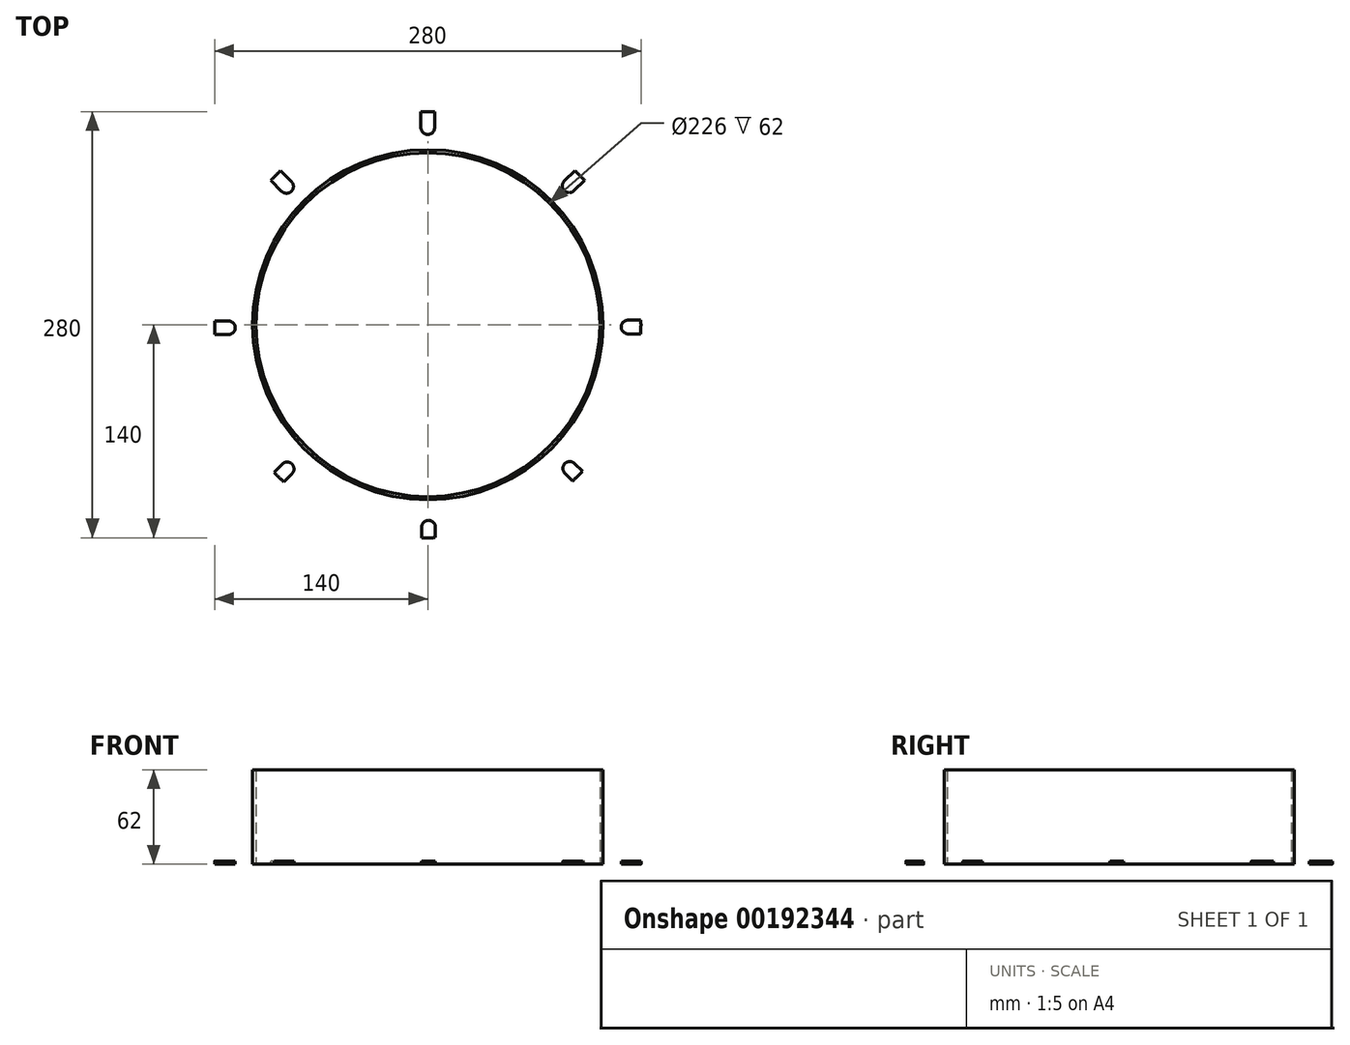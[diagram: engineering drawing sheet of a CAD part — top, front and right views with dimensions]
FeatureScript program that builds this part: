
annotation { "Feature Type Name" : "Feature", "Feature Type Description" : "" }
export const myFeature = defineFeature(function(context is Context, id is Id, definition is map)
    precondition{}
    {
        {
            var Q0;
            Q0=qCreatedBy(makeId("Top.planeOp"),FACE);
            var sketch = newSketch(context, id + "F0", { "sketchPlane" : qUnion([Q0])});
            skCircle(sketch, "E0", {"center": v(0, 0) * mm, "radius": 140 * mm});
            skCircle(sketch, "E1", {"center": v(0, 0) * mm, "radius": 113 * mm});
            skSolve(sketch);
        }
        {
            var Q0;
            Q0=makeQuery(id+"F0.imprint","IMPRINT",FACE,{"disambiguationData":[TD([[makeQuery(id+"F0.imprint","IMPRINT",EDGE,{"derivedFrom":sQuery(id+"F0.wireOp",EDGE,"E0")}),1.0]])]});
            extrude(context, id + "F1", {"entities" : qUnion([Q0]), "depth" : 2 * mm});
        }
        {
            var Q0;
            Q0=makeQuery(id+"F1.opExtrude","CAP_FACE",FACE,{"disambiguationData":[OSD([sQuery(id+"F0.wireOp",EDGE,"E0"),sQuery(id+"F0.wireOp",EDGE,"E1")])],"isStart":false});
            var sketch = newSketch(context, id + "F2", { "sketchPlane" : qUnion([Q0])});
            skCircle(sketch, "E2.0", {"center": v(0, 0) * mm, "radius": 113 * mm});
            skCircle(sketch, "E3.0", {"center": v(0, 0) * mm, "radius": 115 * mm});
            skSolve(sketch);
        }
        {
            var Q0;
            Q0=makeQuery(id+"F2.imprint","IMPRINT",FACE,{"disambiguationData":[TD([[makeQuery(id+"F2.imprint","IMPRINT",EDGE,{"derivedFrom":sQuery(id+"F2.wireOp",EDGE,"E2.0")}),-1.0]])]});
            extrude(context, id + "F3", {"entities" : qUnion([Q0]), "operationType" : NewBodyOperationType.ADD, "depth" : 60 * mm});
        }
        {
            var Q0;
            Q0=makeQuery(id+"F1.opExtrude","CAP_FACE",FACE,{"disambiguationData":[OSD([sQuery(id+"F0.wireOp",EDGE,"E0"),sQuery(id+"F0.wireOp",EDGE,"E1")])],"isStart":false});
            var sketch = newSketch(context, id + "F4", { "sketchPlane" : qUnion([Q0])});
            skLineSegment(sketch, "E4", {"start": v(0, 129.5) * mm, "end": v(0, 140) * mm});
            skArc(sketch, "E5.0.startCap", {"start": v(4.5, 129.5) * mm, "mid": v(0, 125) * mm, "end": v(-4.5, 129.5) * mm});
            skArc(sketch, "E5.0.endCap", {"start": v(-4.5, 140) * mm, "mid": v(0, 144.5) * mm, "end": v(4.5, 140) * mm});
            skLineSegment(sketch, "E5.0.left", {"start": v(-4.5, 129.5) * mm, "end": v(-4.5, 140) * mm});
            skLineSegment(sketch, "E5.0.right", {"start": v(4.5, 129.5) * mm, "end": v(4.5, 140) * mm});
            skArc(sketch, "E6.1.0", {"start": v(-103.34, 95.12) * mm, "mid": v(-103.34, 101.49) * mm, "end": v(-96.98, 101.49) * mm});
            skLineSegment(sketch, "E6.1.1", {"start": v(-89.55, 94.06) * mm, "end": v(-96.98, 101.49) * mm});
            skArc(sketch, "E6.1.2", {"start": v(-89.55, 94.06) * mm, "mid": v(-89.55, 87.7) * mm, "end": v(-95.92, 87.7) * mm});
            skLineSegment(sketch, "E6.1.3", {"start": v(-95.92, 87.7) * mm, "end": v(-103.34, 95.12) * mm});
            skArc(sketch, "E6.2.0", {"start": v(-141.5, -6.5) * mm, "mid": v(-146, -2) * mm, "end": v(-141.5, 2.5) * mm});
            skLineSegment(sketch, "E6.2.1", {"start": v(-131, 2.5) * mm, "end": v(-141.5, 2.5) * mm});
            skArc(sketch, "E6.2.2", {"start": v(-131, 2.5) * mm, "mid": v(-126.5, -2) * mm, "end": v(-131, -6.5) * mm});
            skLineSegment(sketch, "E6.2.3", {"start": v(-131, -6.5) * mm, "end": v(-141.5, -6.5) * mm});
            skArc(sketch, "E6.3.0", {"start": v(-96.62, -105.34) * mm, "mid": v(-102.99, -105.34) * mm, "end": v(-102.99, -98.98) * mm});
            skLineSegment(sketch, "E6.3.1", {"start": v(-95.56, -91.55) * mm, "end": v(-102.99, -98.98) * mm});
            skArc(sketch, "E6.3.2", {"start": v(-95.56, -91.55) * mm, "mid": v(-89.2, -91.55) * mm, "end": v(-89.2, -97.92) * mm});
            skLineSegment(sketch, "E6.3.3", {"start": v(-89.2, -97.92) * mm, "end": v(-96.62, -105.34) * mm});
            skArc(sketch, "E6.4.0", {"start": v(5, -143.5) * mm, "mid": v(0.5, -148) * mm, "end": v(-4, -143.5) * mm});
            skLineSegment(sketch, "E6.4.1", {"start": v(-4, -133) * mm, "end": v(-4, -143.5) * mm});
            skArc(sketch, "E6.4.2", {"start": v(-4, -133) * mm, "mid": v(0.5, -128.5) * mm, "end": v(5, -133) * mm});
            skLineSegment(sketch, "E6.4.3", {"start": v(5, -133) * mm, "end": v(5, -143.5) * mm});
            skArc(sketch, "E6.5.0", {"start": v(103.84, -98.62) * mm, "mid": v(103.84, -104.99) * mm, "end": v(97.48, -104.99) * mm});
            skLineSegment(sketch, "E6.5.1", {"start": v(90.05, -97.56) * mm, "end": v(97.48, -104.99) * mm});
            skArc(sketch, "E6.5.2", {"start": v(90.05, -97.56) * mm, "mid": v(90.05, -91.2) * mm, "end": v(96.42, -91.2) * mm});
            skLineSegment(sketch, "E6.5.3", {"start": v(96.42, -91.2) * mm, "end": v(103.84, -98.62) * mm});
            skArc(sketch, "E6.6.0", {"start": v(142, 3) * mm, "mid": v(146.5, -1.5) * mm, "end": v(142, -6) * mm});
            skLineSegment(sketch, "E6.6.1", {"start": v(131.5, -6) * mm, "end": v(142, -6) * mm});
            skArc(sketch, "E6.6.2", {"start": v(131.5, -6) * mm, "mid": v(127, -1.5) * mm, "end": v(131.5, 3) * mm});
            skLineSegment(sketch, "E6.6.3", {"start": v(131.5, 3) * mm, "end": v(142, 3) * mm});
            skArc(sketch, "E6.7.0", {"start": v(97.12, 101.84) * mm, "mid": v(103.49, 101.84) * mm, "end": v(103.49, 95.48) * mm});
            skLineSegment(sketch, "E6.7.1", {"start": v(96.06, 88.05) * mm, "end": v(103.49, 95.48) * mm});
            skArc(sketch, "E6.7.2", {"start": v(96.06, 88.05) * mm, "mid": v(89.7, 88.05) * mm, "end": v(89.7, 94.42) * mm});
            skLineSegment(sketch, "E6.7.3", {"start": v(89.7, 94.42) * mm, "end": v(97.12, 101.84) * mm});
            skPoint(sketch, "E6.center", {"position": v(0.25, -1.75) * mm});
            skSolve(sketch);
        }
        {
            var Q0;
            {var subQ4=sQuery(id+"F4.wireOp",EDGE,"E5.0.startCap");Q0=makeQuery(id+"F4.imprint","IMPRINT",FACE,{"disambiguationData":[TD([[makeQuery(id+"F4.imprint","IMPRINT",EDGE,{"derivedFrom":subQ4}),-1.0]])]});}
            var Q1;
            {var subQ0=sQuery(id+"F4.wireOp",EDGE,"E6.7.2");Q1=makeQuery(id+"F4.imprint","IMPRINT",FACE,{"disambiguationData":[TD([[makeQuery(id+"F4.imprint","IMPRINT",EDGE,{"derivedFrom":subQ0}),-1.0]])]});}
            var Q2;
            {var subQ0=sQuery(id+"F4.wireOp",EDGE,"E6.6.2");Q2=makeQuery(id+"F4.imprint","IMPRINT",FACE,{"disambiguationData":[TD([[makeQuery(id+"F4.imprint","IMPRINT",EDGE,{"derivedFrom":subQ0}),-1.0]])]});}
            var Q3;
            {var subQ0=sQuery(id+"F4.wireOp",EDGE,"E6.5.2");Q3=makeQuery(id+"F4.imprint","IMPRINT",FACE,{"disambiguationData":[TD([[makeQuery(id+"F4.imprint","IMPRINT",EDGE,{"derivedFrom":subQ0}),-1.0]])]});}
            var Q4;
            {var subQ0=sQuery(id+"F4.wireOp",EDGE,"E6.4.2");Q4=makeQuery(id+"F4.imprint","IMPRINT",FACE,{"disambiguationData":[TD([[makeQuery(id+"F4.imprint","IMPRINT",EDGE,{"derivedFrom":subQ0}),-1.0]])]});}
            var Q5;
            {var subQ0=sQuery(id+"F4.wireOp",EDGE,"E6.3.2");Q5=makeQuery(id+"F4.imprint","IMPRINT",FACE,{"disambiguationData":[TD([[makeQuery(id+"F4.imprint","IMPRINT",EDGE,{"derivedFrom":subQ0}),-1.0]])]});}
            var Q6;
            {var subQ0=sQuery(id+"F4.wireOp",EDGE,"E6.2.2");Q6=makeQuery(id+"F4.imprint","IMPRINT",FACE,{"disambiguationData":[TD([[makeQuery(id+"F4.imprint","IMPRINT",EDGE,{"derivedFrom":subQ0}),-1.0]])]});}
            var Q7;
            {var subQ0=sQuery(id+"F4.wireOp",EDGE,"E6.1.2");Q7=makeQuery(id+"F4.imprint","IMPRINT",FACE,{"disambiguationData":[TD([[makeQuery(id+"F4.imprint","IMPRINT",EDGE,{"derivedFrom":subQ0}),-1.0]])]});}
            extrude(context, id + "F5", {"entities" : qUnion([Q0, Q1, Q2, Q3, Q4, Q5, Q6, Q7]), "operationType" : NewBodyOperationType.REMOVE, "endBound" : BoundingType.THROUGH_ALL, "oppositeDirection" : true, "depth" : 25 * mm});
        }
    });
